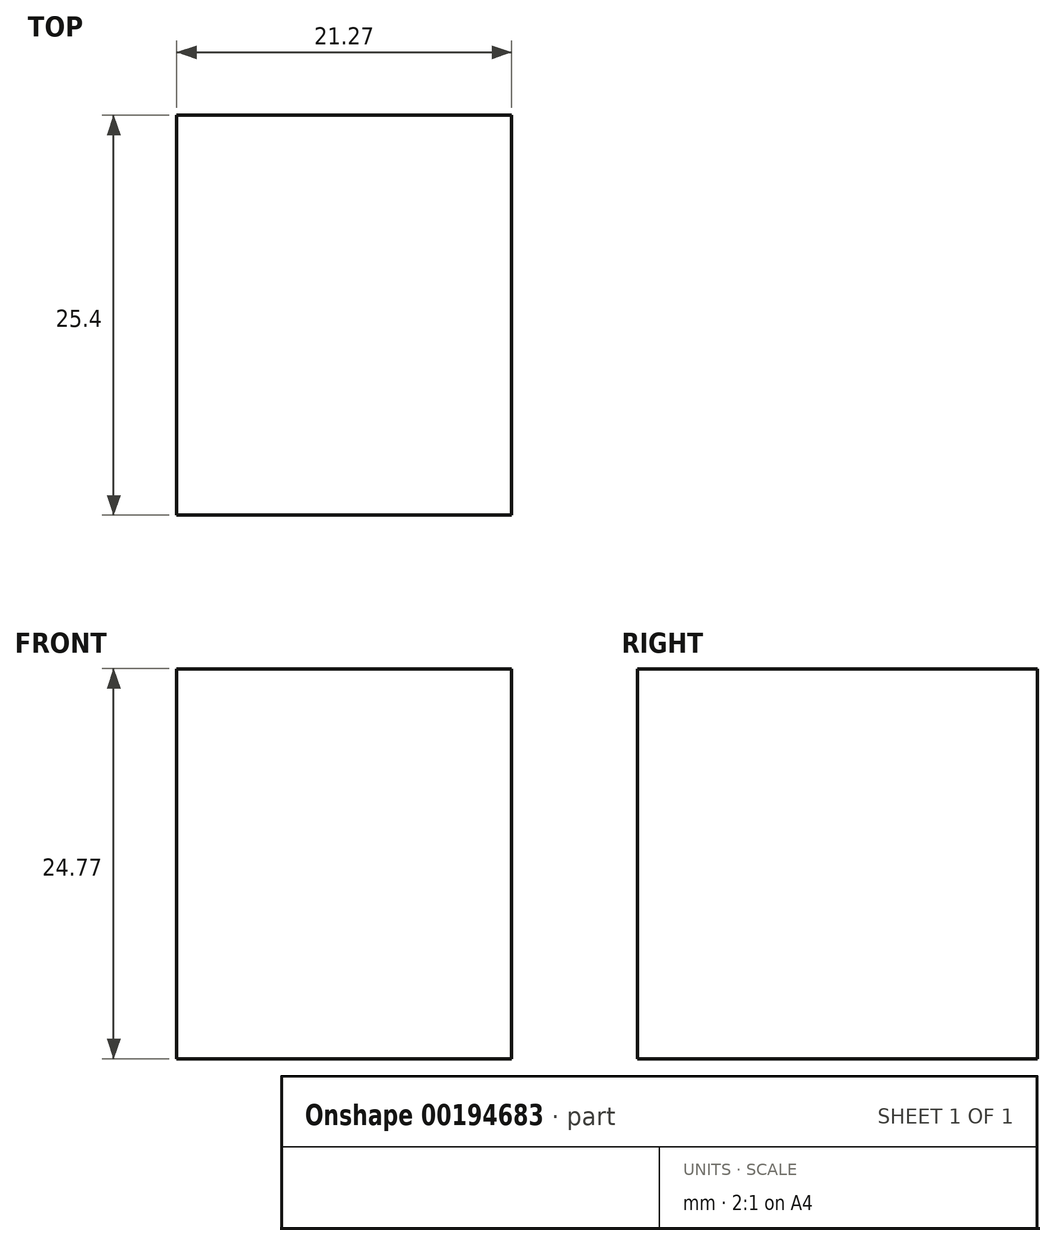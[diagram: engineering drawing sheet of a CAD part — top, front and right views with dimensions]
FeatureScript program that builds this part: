
annotation { "Feature Type Name" : "Feature", "Feature Type Description" : "" }
export const myFeature = defineFeature(function(context is Context, id is Id, definition is map)
    precondition{}
    {
        {
            var Q0;
            Q0=qCreatedBy(makeId("Front.planeOp"),FACE);
            var sketch = newSketch(context, id + "F0", { "sketchPlane" : qUnion([Q0])});
            skLineSegment(sketch, "E0.bottom", {"start": v(0, 0) * mm, "end": v(21.27, 0) * mm});
            skLineSegment(sketch, "E0.top", {"start": v(0, 24.77) * mm, "end": v(21.27, 24.77) * mm});
            skLineSegment(sketch, "E0.left", {"start": v(0, 0) * mm, "end": v(0, 24.77) * mm});
            skLineSegment(sketch, "E0.right", {"start": v(21.27, 0) * mm, "end": v(21.27, 24.77) * mm});
            skSolve(sketch);
        }
        {
            var Q0;
            Q0=makeQuery(id+"F0.imprint","IMPRINT",FACE,{"disambiguationData":[TD([[makeQuery(id+"F0.imprint","IMPRINT",EDGE,{"derivedFrom":sQuery(id+"F0.wireOp",EDGE,"E0.bottom")}),1.0]])]});
            extrude(context, id + "F1", {"entities" : qUnion([Q0]), "depth" : 25.4 * mm});
        }
    });
